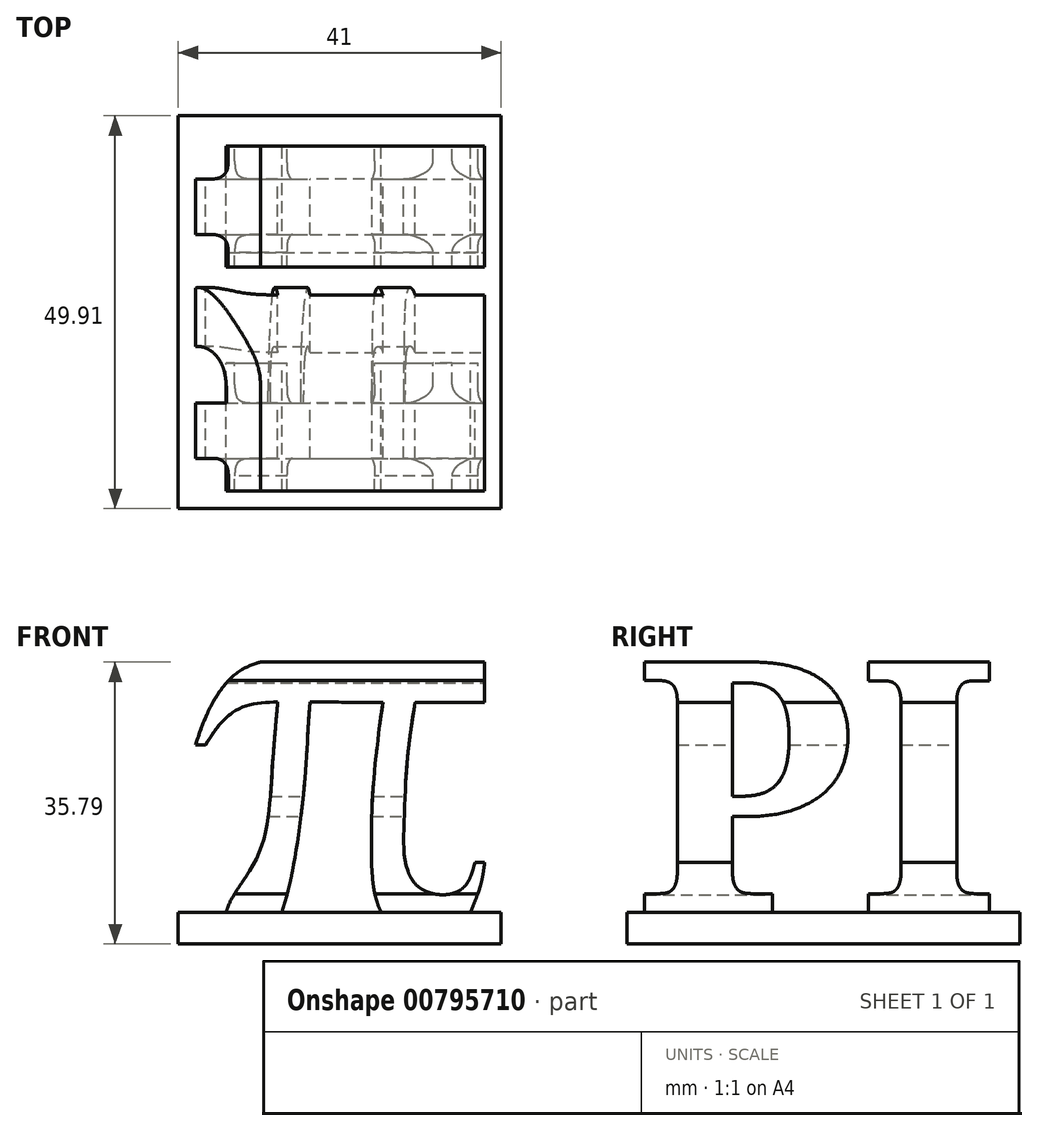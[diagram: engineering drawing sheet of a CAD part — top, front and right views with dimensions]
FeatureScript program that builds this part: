
annotation { "Feature Type Name" : "Feature", "Feature Type Description" : "" }
export const myFeature = defineFeature(function(context is Context, id is Id, definition is map)
    precondition{}
    {
        {
            var Q0;
            Q0=qCreatedBy(makeId("Front.planeOp"),FACE);
            var sketch = newSketch(context, id + "F0", { "sketchPlane" : qUnion([Q0])});
            skLineSegment(sketch, "E0.bottom", {"start": v(11, 4) * mm, "end": v(52, 4) * mm});
            skLineSegment(sketch, "E0.top", {"start": v(11, 8) * mm, "end": v(17.08, 8) * mm});
            skLineSegment(sketch, "E0.left", {"start": v(11, 4) * mm, "end": v(11, 8) * mm});
            skLineSegment(sketch, "E0.right", {"start": v(52, 4) * mm, "end": v(52, 8) * mm});
            skFitSpline(sketch, "E1", {"points": [v(48.1, 8) * mm, v(49.38, 11.37) * mm, v(49.93, 14.34) * mm], "startDerivative": vector(2.78, 6.52) * mm, "endDerivative": vector(0.83, 6.16) * mm});
            skFitSpline(sketch, "E2", {"points": [v(48.67, 14.34) * mm, v(47.45, 11.37) * mm, v(44.85, 10.24) * mm, v(41.46, 11.28) * mm, v(39.86, 14.34) * mm, v(39.67, 19.15) * mm, v(40.1, 27.36) * mm, v(41.08, 34.67) * mm], "startDerivative": vector(-7.2, -27.9) * mm, "endDerivative": vector(6.22, 39) * mm});
            skFitSpline(sketch, "E3", {"points": [v(36.98, 34.67) * mm, v(35.75, 23.82) * mm, v(35.56, 14.34) * mm, v(35.99, 10.24) * mm, v(36.74, 8) * mm], "startDerivative": vector(-4.39, -32.44) * mm, "endDerivative": vector(5.43, -13.7) * mm});
            skFitSpline(sketch, "E4", {"points": [v(24.15, 8) * mm, v(25.43, 12.83) * mm, v(27.08, 24.81) * mm, v(27.74, 34.71) * mm], "startDerivative": vector(5.1, 16.6) * mm, "endDerivative": vector(2.54, 26.42) * mm});
            skFitSpline(sketch, "E5", {"points": [v(23.63, 34.71) * mm, v(22.97, 26.74) * mm, v(22.55, 21.18) * mm, v(21.23, 15.47) * mm, v(18.68, 11.18) * mm, v(17.4, 8.97) * mm, v(17.08, 8) * mm], "startDerivative": vector(-3.28, -36.85) * mm, "endDerivative": vector(-3.12, -11.04) * mm});
            skFitSpline(sketch, "E6", {"points": [v(14.49, 29.3) * mm, v(16.66, 32.3) * mm, v(19.63, 34.24) * mm, v(23.63, 34.71) * mm], "startDerivative": vector(6, 9.65) * mm, "endDerivative": vector(12.1, 0.31) * mm});
            skFitSpline(sketch, "E7", {"points": [v(13.2, 29.3) * mm, v(14.88, 33.68) * mm, v(17.63, 37.71) * mm, v(20.1, 39.34) * mm, v(22.62, 40) * mm, v(27.32, 40) * mm, v(49.93, 40) * mm], "startDerivative": vector(8.77, 26.07) * mm, "endDerivative": vector(86.32, 0) * mm});
            skLineSegment(sketch, "E8", {"start": v(48.67, 14.34) * mm, "end": v(49.93, 14.34) * mm});
            skLineSegment(sketch, "E9", {"start": v(41.08, 34.67) * mm, "end": v(49.93, 34.67) * mm});
            skLineSegment(sketch, "E10", {"start": v(49.93, 40) * mm, "end": v(49.93, 34.67) * mm});
            skLineSegment(sketch, "E11", {"start": v(36.98, 34.67) * mm, "end": v(27.74, 34.71) * mm});
            skLineSegment(sketch, "E12", {"start": v(14.49, 29.3) * mm, "end": v(13.2, 29.3) * mm});
            skLineSegment(sketch, "E13.trimOffspring", {"start": v(48.1, 8) * mm, "end": v(52, 8) * mm});
            skLineSegment(sketch, "E14.trimOffspring", {"start": v(24.15, 8) * mm, "end": v(36.74, 8) * mm});
            skSolve(sketch);
        }
        {
            var Q0;
            Q0=makeQuery(id+"F0.imprint","IMPRINT",FACE,{"disambiguationData":[TD([[makeQuery(id+"F0.imprint","IMPRINT",EDGE,{"derivedFrom":sQuery(id+"F0.wireOp",EDGE,"E0.bottom")}),1.0]])]});
            extrude(context, id + "F1", {"entities" : qUnion([Q0]), "depth" : 60 * mm, "offsetDistance" : 25 * mm});
        }
        {
            var Q0;
            Q0=makeQuery(id+"F1.opExtrude","SWEPT_FACE",FACE,{"disambiguationData":[OSD([sQuery(id+"F0.wireOp",EDGE,"E0.right")])]});
            cPlane(context, id + "F2", {"entities" : qUnion([Q0]), "cplaneType" : CPlaneType.OFFSET, "offset" : 0 * mm, "width" : 150 * mm, "height" : 150 * mm});
        }
        {
            var Q0;
            Q0=qCreatedBy(id+"F2.planeOp",FACE);
            var sketch = newSketch(context, id + "F3", { "sketchPlane" : qUnion([Q0])});
            skLineSegment(sketch, "E15.0.0", {"start": v(0, 34.67) * mm, "end": v(0, 40) * mm});
            skLineSegment(sketch, "E15.0.1", {"start": v(0, 40) * mm, "end": v(-60, 40) * mm});
            skLineSegment(sketch, "E15.0.2", {"start": v(-60, 40) * mm, "end": v(-60, 34.67) * mm});
            skLineSegment(sketch, "E16.0.0", {"start": v(0, 4) * mm, "end": v(0, 8) * mm});
            skLineSegment(sketch, "E16.0.2", {"start": v(-60, 8) * mm, "end": v(-60, 4) * mm});
            skLineSegment(sketch, "E16.0.3", {"start": v(-60, 4) * mm, "end": v(0, 4) * mm});
            skFitSpline(sketch, "E17.0.0", {"points": [v(0, 8) * mm, v(0, 9.13) * mm, v(0, 11.3) * mm, v(0, 13.36) * mm, v(0, 14.34) * mm]});
            skFitSpline(sketch, "E17.0.2", {"points": [v(-60, 14.34) * mm, v(-60, 13.36) * mm, v(-60, 11.3) * mm, v(-60, 9.13) * mm, v(-60, 8) * mm]});
            skLineSegment(sketch, "E18.0.0", {"start": v(-60, 34.67) * mm, "end": v(-60, 40) * mm});
            skFitSpline(sketch, "E18.0.3", {"points": [v(-60, 29.3) * mm, v(-60, 30.36) * mm, v(-60, 32.46) * mm, v(-60, 34.6) * mm, v(-60, 34.68) * mm, v(-60, 34.71) * mm]});
            skFitSpline(sketch, "E18.0.4", {"points": [v(-60, 34.71) * mm, v(-60, 31.92) * mm, v(-60, 26.8) * mm, v(-60, 21.27) * mm, v(-60, 15.38) * mm, v(-60, 11.38) * mm, v(-60, 9.07) * mm, v(-60, 8.3) * mm, v(-60, 8) * mm]});
            skLineSegment(sketch, "E18.0.8", {"start": v(-60, 4) * mm, "end": v(-60, 8) * mm});
            skFitSpline(sketch, "E18.0.10", {"points": [v(-60, 8) * mm, v(-60, 9.13) * mm, v(-60, 11.3) * mm, v(-60, 13.36) * mm, v(-60, 14.34) * mm]});
            skLineSegment(sketch, "E19.0.0", {"start": v(0, 40) * mm, "end": v(0, 34.67) * mm});
            skFitSpline(sketch, "E19.0.2", {"points": [v(0, 34.67) * mm, v(0, 26.52) * mm, v(0, 18.38) * mm, v(0, 10.23) * mm]});
            skFitSpline(sketch, "E19.0.4", {"points": [v(0, 14.34) * mm, v(0, 13.36) * mm, v(0, 11.3) * mm, v(0, 9.13) * mm, v(0, 8) * mm]});
            skLineSegment(sketch, "E19.0.6", {"start": v(0, 8) * mm, "end": v(0, 4) * mm});
            skFitSpline(sketch, "E19.0.10", {"points": [v(0, 8) * mm, v(0, 8.3) * mm, v(0, 9.07) * mm, v(0, 11.38) * mm, v(0, 15.38) * mm, v(0, 21.27) * mm, v(0, 26.8) * mm, v(0, 31.92) * mm, v(0, 34.71) * mm]});
            skFitSpline(sketch, "E19.0.11", {"points": [v(0, 34.71) * mm, v(0, 34.68) * mm, v(0, 34.6) * mm, v(0, 32.46) * mm, v(0, 30.36) * mm, v(0, 29.3) * mm]});
            skFitSpline(sketch, "E19.0.13", {"points": [v(0, 29.3) * mm, v(0, 32.88) * mm, v(0, 36.48) * mm, v(0, 40.07) * mm]});
            skText(sketch, "E20", { "text": "PI", "fontName": "NotoSerif-Bold.ttf"});
            skLineSegment(sketch, "E21.0.1", {"start": v(0, 8) * mm, "end": v(-60, 8) * mm});
            skLineSegment(sketch, "E22", {"start": v(-10.1, 8) * mm, "end": v(-10.1, 4) * mm});
            const initialGuessF3  = {"E20": [-0.059, 0.008, 1, 0, 0.03206]};
            skSetInitialGuess(sketch, initialGuessF3);
            skSolve(sketch);
        }
        {
            var Q0;
            {var subQ6=sQuery(id+"F3.wireOp",EDGE,"E16.0.2");Q0=makeQuery(id+"F3.imprint","IMPRINT",FACE,{"disambiguationData":[TD([[makeQuery(id+"F3.imprint","IMPRINT",EDGE,{"derivedFrom":subQ6}),1.0]])]});}
            var Q1;
            {var subQ0=sQuery(id+"F3.wireOp",EDGE,"E20.sketch_text.stroke-42");Q1=makeQuery(id+"F3.imprint","IMPRINT",FACE,{"disambiguationData":[TD([[makeQuery(id+"F3.imprint","IMPRINT",EDGE,{"derivedFrom":subQ0}),-1.0]])]});}
            var Q2;
            Q2=makeQuery(id+"F3.imprint","IMPRINT",FACE,{"disambiguationData":[TD([[makeQuery(id+"F3.imprint","IMPRINT",EDGE,{"derivedFrom":sQuery(id+"F3.wireOp",EDGE,"E20.sketch_text.stroke-0")}),-1.0]])]});
            extrude(context, id + "F4", {"entities" : qUnion([Q0, Q1, Q2]), "operationType" : NewBodyOperationType.INTERSECT, "endBound" : BoundingType.THROUGH_ALL, "oppositeDirection" : true, "depth" : 25 * mm, "offsetDistance" : 25 * mm});
        }
    });
